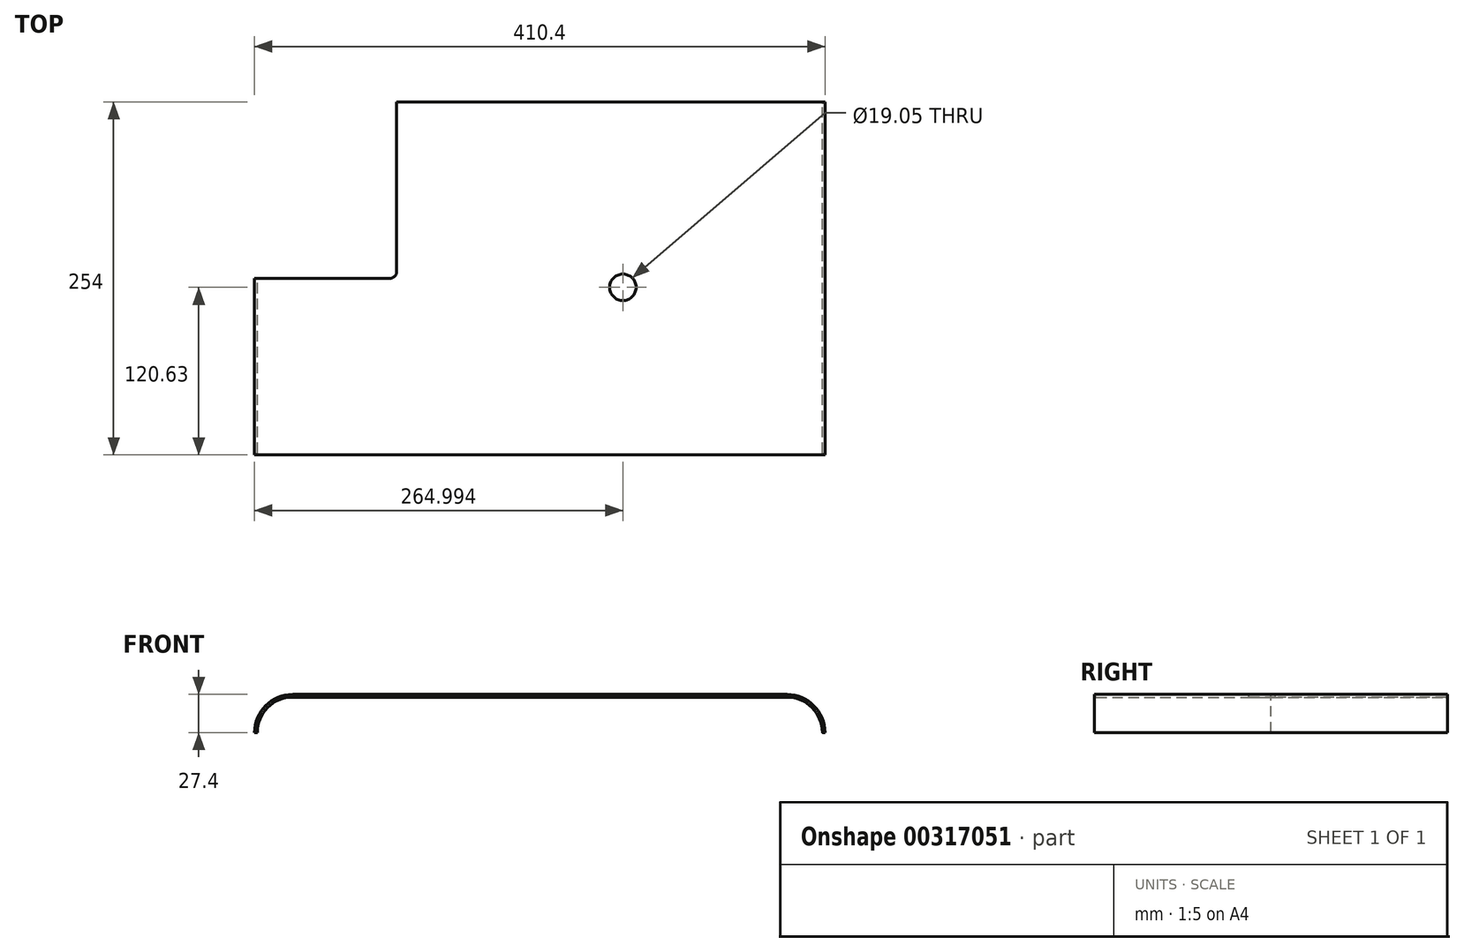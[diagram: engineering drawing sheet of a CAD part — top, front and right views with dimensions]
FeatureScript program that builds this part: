
annotation { "Feature Type Name" : "Feature", "Feature Type Description" : "" }
export const myFeature = defineFeature(function(context is Context, id is Id, definition is map)
    precondition{}
    {
        {
            var Q0;
            Q0=qCreatedBy(makeId("Front.planeOp"),FACE);
            var sketch = newSketch(context, id + "F0", { "sketchPlane" : qUnion([Q0])});
            skLineSegment(sketch, "E0", {"start": v(0, 0) * mm, "end": v(355.6, 0) * mm});
            skLineSegment(sketch, "E1", {"start": v(0, 101.1) * mm, "end": v(0, -98.66) * mm, "construction": true});
            skPoint(sketch, "E2", {"position": v(0, -25.4) * mm});
            skArc(sketch, "E3", {"start": v(0, 0) * mm, "mid": v(-17.96, -7.44) * mm, "end": v(-25.4, -25.4) * mm});
            skPoint(sketch, "E4", {"position": v(-25.4, -25.4) * mm});
            skLineSegment(sketch, "E5", {"start": v(177.8, 79.9) * mm, "end": v(177.8, -94.58) * mm, "construction": true});
            skPoint(sketch, "E5.startSnap0", {"position": v(177.8, 0) * mm});
            skArc(sketch, "E6.MirrorCS", {"start": v(355.6, 0) * mm, "mid": v(373.56, -7.44) * mm, "end": v(381, -25.4) * mm});
            skArc(sketch, "E7.0", {"start": v(0, 2) * mm, "mid": v(-19.37, -6.03) * mm, "end": v(-27.4, -25.4) * mm});
            skLineSegment(sketch, "E7.1", {"start": v(0, 2) * mm, "end": v(355.6, 2) * mm});
            skArc(sketch, "E7.2", {"start": v(355.6, 2) * mm, "mid": v(374.97, -6.03) * mm, "end": v(383, -25.4) * mm});
            skLineSegment(sketch, "E8", {"start": v(-25.4, -25.4) * mm, "end": v(-27.4, -25.4) * mm});
            skLineSegment(sketch, "E9", {"start": v(383, -25.4) * mm, "end": v(381, -25.4) * mm});
            skSolve(sketch);
        }
        {
            var Q0;
            Q0 = qSketchRegion(id + "F0", true);
            extrude(context, id + "F1", {"entities" : qUnion([Q0]), "depth" : 254 * mm});
        }
        {
            var Q0;
            Q0=makeQuery(id+"F1.opExtrude","SWEPT_FACE",FACE,{"disambiguationData":[OSD([sQuery(id+"F0.wireOp",EDGE,"E7.1")])]});
            var sketch = newSketch(context, id + "F2", { "sketchPlane" : qUnion([Q0])});
            skLineSegment(sketch, "E10.bottom", {"start": v(50.8, 0) * mm, "end": v(-52.07, 0) * mm});
            skLineSegment(sketch, "E10.top", {"start": v(69.85, -127) * mm, "end": v(0, -127) * mm});
            skLineSegment(sketch, "E10.left", {"start": v(74.93, -25.4) * mm, "end": v(74.93, -121.92) * mm});
            skLineSegment(sketch, "E10.right", {"start": v(-52.07, 0) * mm, "end": v(-52.07, -101.6) * mm});
            skPoint(sketch, "E11.visualSharp", {"position": v(74.93, -127) * mm});
            skArc(sketch, "E11.filletArc", {"start": v(69.85, -127) * mm, "mid": v(73.44, -125.51) * mm, "end": v(74.93, -121.92) * mm});
            skPoint(sketch, "E12.visualSharp", {"position": v(74.93, 0) * mm});
            skPoint(sketch, "E13.visualSharp", {"position": v(-52.07, -127) * mm});
            skLineSegment(sketch, "E14", {"start": v(50.8, 0) * mm, "end": v(74.93, 0) * mm});
            skLineSegment(sketch, "E15", {"start": v(74.93, -25.4) * mm, "end": v(74.93, 0) * mm});
            skLineSegment(sketch, "E16", {"start": v(0, -127) * mm, "end": v(-52.07, -127) * mm});
            skLineSegment(sketch, "E17", {"start": v(-52.07, -101.6) * mm, "end": v(-52.07, -127) * mm});
            skSolve(sketch);
        }
        {
            var Q0;
            Q0 = qSketchRegion(id + "F2", true);
            extrude(context, id + "F3", {"entities" : qUnion([Q0]), "operationType" : NewBodyOperationType.REMOVE, "endBound" : BoundingType.THROUGH_ALL, "oppositeDirection" : true, "depth" : 25.4 * mm});
        }
        {
            var Q0;
            Q0=qCreatedBy(makeId("Right.planeOp"),FACE);
            var sketch = newSketch(context, id + "F4", { "sketchPlane" : qUnion([Q0])});
            skLineSegment(sketch, "E18.bottom", {"start": v(0, 0) * mm, "end": v(-101.6, 0) * mm});
            skLineSegment(sketch, "E18.top", {"start": v(0, -38.1) * mm, "end": v(-101.6, -38.1) * mm});
            skLineSegment(sketch, "E18.left", {"start": v(0, 0) * mm, "end": v(0, -38.1) * mm});
            skLineSegment(sketch, "E18.right", {"start": v(-101.6, 0) * mm, "end": v(-101.6, -38.1) * mm});
            skSolve(sketch);
        }
        {
            var Q0;
            Q0=makeQuery(id+"F4.imprint","IMPRINT",FACE,{"disambiguationData":[TD([[makeQuery(id+"F4.imprint","IMPRINT",EDGE,{"derivedFrom":sQuery(id+"F4.wireOp",EDGE,"E18.bottom")}),1.0]])]});
            extrude(context, id + "F5", {"entities" : qUnion([Q0]), "operationType" : NewBodyOperationType.REMOVE, "oppositeDirection" : true, "depth" : 42.42 * mm});
        }
        {
            var Q0;
            Q0=makeQuery(id+"F1.opExtrude","CAP_EDGE",EDGE,{"disambiguationData":[OSD([sQuery(id+"F0.wireOp",EDGE,"E0")])],"isStart":false});
            var Q1;
            Q1=makeQuery(id+"F1.opExtrude","CAP_EDGE",EDGE,{"disambiguationData":[OSD([sQuery(id+"F0.wireOp",EDGE,"E0")])],"isStart":true});
            fillet(context, id + "F6", {"entities" : qUnion([Q0, Q1]), "radius" : 1.27 * mm, "tangentPropagation" : true, "allowEdgeOverflow" : false});
        }
        {
            var Q0;
            Q0=makeQuery(id+"F1.opExtrude","SWEPT_FACE",FACE,{"disambiguationData":[OSD([sQuery(id+"F0.wireOp",EDGE,"E7.1")])]});
            var sketch = newSketch(context, id + "F7", { "sketchPlane" : qUnion([Q0])});
            skLineSegment(sketch, "E19", {"start": v(-154.71, -133.37) * mm, "end": v(498.5, -133.37) * mm, "construction": true});
            skCircle(sketch, "E20", {"center": v(237.6, -133.37) * mm, "radius": 9.53 * mm});
            skSolve(sketch);
        }
        {
            var Q0;
            Q0 = qSketchRegion(id + "F7", true);
            extrude(context, id + "F8", {"entities" : qUnion([Q0]), "operationType" : NewBodyOperationType.REMOVE, "endBound" : BoundingType.THROUGH_ALL, "oppositeDirection" : true, "depth" : 25.4 * mm});
        }
    });
